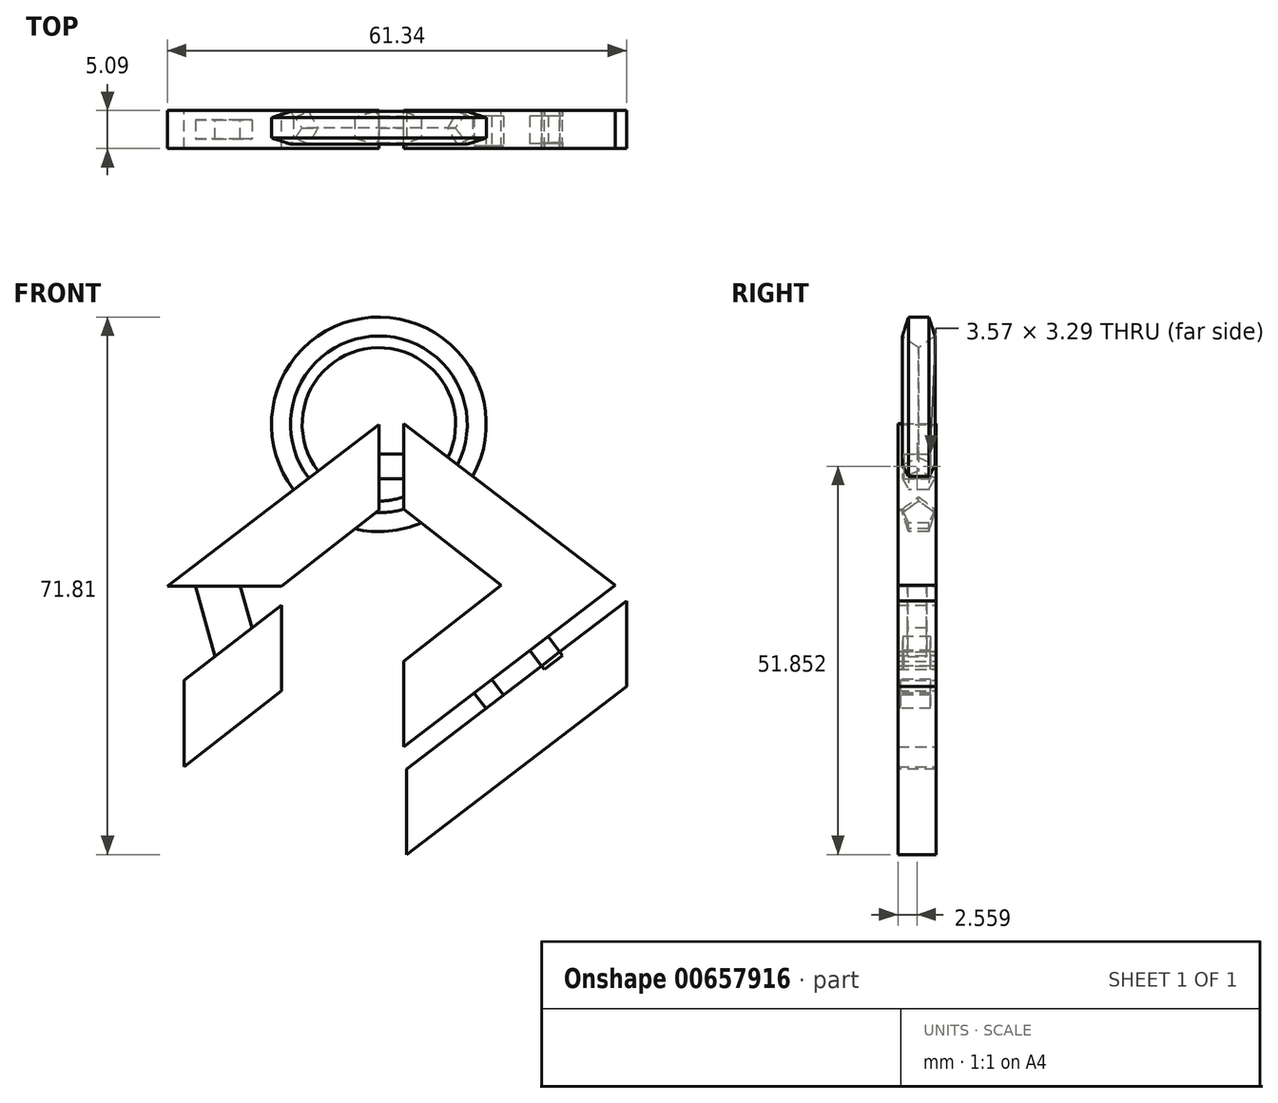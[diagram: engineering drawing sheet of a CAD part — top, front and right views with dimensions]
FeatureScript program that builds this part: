
annotation { "Feature Type Name" : "Feature", "Feature Type Description" : "" }
export const myFeature = defineFeature(function(context is Context, id is Id, definition is map)
    precondition{}
    {
        {
            var Q0;
            Q0=qCreatedBy(makeId("Front.planeOp"),FACE);
            var sketch = newSketch(context, id + "F0", { "sketchPlane" : qUnion([Q0])});
            skLineSegment(sketch, "E0", {"start": v(1.57, 49.1) * mm, "end": v(1.57, 37.68) * mm});
            skLineSegment(sketch, "E1", {"start": v(1.57, 37.68) * mm, "end": v(14.59, 27.51) * mm});
            skLineSegment(sketch, "E2", {"start": v(14.59, 27.51) * mm, "end": v(29.83, 27.51) * mm});
            skLineSegment(sketch, "E3", {"start": v(1.57, 49.1) * mm, "end": v(29.83, 27.51) * mm});
            skSolve(sketch);
        }
        {
            var Q0;
            Q0=makeQuery(id+"F0.imprint","IMPRINT",FACE,{"disambiguationData":[TD([[makeQuery(id+"F0.imprint","IMPRINT",EDGE,{"derivedFrom":sQuery(id+"F0.wireOp",EDGE,"E0")}),1.0]])]});
            extrude(context, id + "F1", {"entities" : qUnion([Q0]), "depth" : 5.08 * mm, "offsetDistance" : 25.4 * mm});
        }
        {
            var Q0;
            Q0=makeQuery(id+"F1.opExtrude","SWEPT_BODY",BODY,{"disambiguationData":[OSD([sQuery(id+"F0.wireOp",EDGE,"E0"),sQuery(id+"F0.wireOp",EDGE,"E1"),sQuery(id+"F0.wireOp",EDGE,"E2"),sQuery(id+"F0.wireOp",EDGE,"E3")])]});
            var Q1;
            Q1=makeQuery(id+"F1.opExtrude","SWEPT_FACE",FACE,{"disambiguationData":[OSD([sQuery(id+"F0.wireOp",EDGE,"E2")])]});
            mirror(context, id + "F2", {"operationType" : NewBodyOperationType.ADD, "entities" : qUnion([Q0]), "mirrorPlane" : qUnion([Q1])});
        }
        {
            var Q0;
            Q0=makeQuery(id+"F1.opExtrude","SWEPT_FACE",FACE,{"disambiguationData":[OSD([sQuery(id+"F0.wireOp",EDGE,"E0")])]});
            var sketch = newSketch(context, id + "F3", { "sketchPlane" : qUnion([Q0])});
            skLineSegment(sketch, "E4.bottom", {"start": v(4.3, 45.04) * mm, "end": v(0.74, 45.04) * mm});
            skLineSegment(sketch, "E4.top", {"start": v(4.3, 41.75) * mm, "end": v(0.74, 41.75) * mm});
            skLineSegment(sketch, "E4.left", {"start": v(4.3, 45.04) * mm, "end": v(4.3, 41.75) * mm});
            skLineSegment(sketch, "E4.right", {"start": v(0.74, 45.04) * mm, "end": v(0.74, 41.75) * mm});
            skPoint(sketch, "E4.middle", {"position": v(2.52, 43.4) * mm});
            skPoint(sketch, "E4.middle.positionSnap0", {"position": v(5.08, 43.4) * mm});
            skPoint(sketch, "E4.centerSnap0", {"position": v(5.08, 43.4) * mm});
            skSolve(sketch);
        }
        {
            var Q0;
            Q0=makeQuery(id+"F3.imprint","IMPRINT",FACE,{"disambiguationData":[TD([[makeQuery(id+"F3.imprint","IMPRINT",EDGE,{"derivedFrom":sQuery(id+"F3.wireOp",EDGE,"E4.bottom")}),1.0]])]});
            extrude(context, id + "F4", {"entities" : qUnion([Q0]), "operationType" : NewBodyOperationType.ADD, "depth" : 3.45 * mm, "offsetDistance" : 25.4 * mm});
        }
        {
            var Q0;
            Q0=qCreatedBy(makeId("Front.planeOp"),FACE);
            var sketch = newSketch(context, id + "F5", { "sketchPlane" : qUnion([Q0])});
            skLineSegment(sketch, "E5", {"start": v(0, 0) * mm, "end": v(-1.52, 0) * mm});
            skLineSegment(sketch, "E6", {"start": v(-1.74, 37.58) * mm, "end": v(-1.74, 49) * mm});
            skLineSegment(sketch, "E7", {"start": v(-1.74, 37.58) * mm, "end": v(-14.75, 27.42) * mm});
            skLineSegment(sketch, "E8", {"start": v(-14.75, 27.42) * mm, "end": v(-29.99, 27.42) * mm});
            skLineSegment(sketch, "E9", {"start": v(-29.99, 27.42) * mm, "end": v(-1.74, 49) * mm});
            skLineSegment(sketch, "E10", {"start": v(-14.75, 24.88) * mm, "end": v(-14.75, 13.45) * mm});
            skLineSegment(sketch, "E11", {"start": v(-14.75, 13.45) * mm, "end": v(-27.76, 3.28) * mm});
            skLineSegment(sketch, "E12", {"start": v(-27.76, 3.28) * mm, "end": v(-27.76, 14.82) * mm});
            skLineSegment(sketch, "E13", {"start": v(-27.76, 14.82) * mm, "end": v(-14.75, 24.88) * mm});
            skSolve(sketch);
        }
        {
            var Q0;
            Q0=makeQuery(id+"F5.imprint","IMPRINT",FACE,{"disambiguationData":[TD([[makeQuery(id+"F5.imprint","IMPRINT",EDGE,{"derivedFrom":sQuery(id+"F5.wireOp",EDGE,"E6")}),1.0]])]});
            var Q1;
            Q1=makeQuery(id+"F5.imprint","IMPRINT",FACE,{"disambiguationData":[TD([[makeQuery(id+"F5.imprint","IMPRINT",EDGE,{"derivedFrom":sQuery(id+"F5.wireOp",EDGE,"YTqawJW2-ZtEl-2KsG-vROz-UY6oSMgULrsX")}),-1.0]])]});
            extrude(context, id + "F6", {"entities" : qUnion([Q0, Q1]), "operationType" : NewBodyOperationType.ADD, "depth" : 5.08 * mm, "offsetDistance" : 25.4 * mm});
        }
        {
            var Q0;
            Q0=makeQuery(id+"F2.opPattern","COPY",FACE,{"derivedFrom":makeQuery(id+"F1.opExtrude","SWEPT_FACE",FACE,{"disambiguationData":[OSD([sQuery(id+"F0.wireOp",EDGE,"E3")])]}),"instanceName":"1"});
            var sketch = newSketch(context, id + "F7", { "sketchPlane" : qUnion([Q0])});
            skLineSegment(sketch, "E14.bottom", {"start": v(29.1, 0.71) * mm, "end": v(26.06, 0.71) * mm});
            skLineSegment(sketch, "E14.top", {"start": v(29.1, 4.41) * mm, "end": v(26.06, 4.41) * mm});
            skLineSegment(sketch, "E14.left", {"start": v(29.1, 0.71) * mm, "end": v(29.1, 4.41) * mm});
            skLineSegment(sketch, "E14.right", {"start": v(26.06, 0.71) * mm, "end": v(26.06, 4.41) * mm});
            skPoint(sketch, "E14.middle", {"position": v(27.58, 2.56) * mm});
            skLineSegment(sketch, "E15.bottom", {"start": v(19.67, 0.71) * mm, "end": v(16.7, 0.71) * mm});
            skLineSegment(sketch, "E15.top", {"start": v(19.67, 4.72) * mm, "end": v(16.7, 4.72) * mm});
            skLineSegment(sketch, "E15.left", {"start": v(19.67, 0.71) * mm, "end": v(19.67, 4.72) * mm});
            skLineSegment(sketch, "E15.right", {"start": v(16.7, 0.71) * mm, "end": v(16.7, 4.72) * mm});
            skPoint(sketch, "E15.middle", {"position": v(18.18, 2.72) * mm});
            skSolve(sketch);
        }
        {
            var Q0;
            Q0=makeQuery(id+"F7.imprint","IMPRINT",FACE,{"disambiguationData":[TD([[makeQuery(id+"F7.imprint","IMPRINT",EDGE,{"derivedFrom":sQuery(id+"F7.wireOp",EDGE,"E14.bottom")}),-1.0]])]});
            var Q1;
            Q1=makeQuery(id+"F7.imprint","IMPRINT",FACE,{"disambiguationData":[TD([[makeQuery(id+"F7.imprint","IMPRINT",EDGE,{"derivedFrom":sQuery(id+"F7.wireOp",EDGE,"E15.bottom")}),-1.0]])]});
            extrude(context, id + "F8", {"entities" : qUnion([Q0, Q1]), "operationType" : NewBodyOperationType.ADD, "depth" : 3.17 * mm, "offsetDistance" : 25.4 * mm});
        }
        {
            var Q0;
            Q0=makeQuery(id+"F8.opExtrude","SWEPT_FACE",FACE,{"disambiguationData":[OSD([sQuery(id+"F7.wireOp",EDGE,"E14.top")])]});
            var sketch = newSketch(context, id + "F9", { "sketchPlane" : qUnion([Q0])});
            skPoint(sketch, "E16", {"position": v(31.35, 25.43) * mm});
            skPoint(sketch, "E17", {"position": v(1.96, 2.97) * mm});
            skLineSegment(sketch, "E18", {"start": v(1.96, 2.97) * mm, "end": v(31.35, 25.43) * mm});
            skLineSegment(sketch, "E19", {"start": v(31.35, 25.43) * mm, "end": v(31.35, 14) * mm});
            skLineSegment(sketch, "E20", {"start": v(1.96, 2.97) * mm, "end": v(1.96, -8.46) * mm});
            skLineSegment(sketch, "E21", {"start": v(1.96, -8.46) * mm, "end": v(31.35, 14) * mm});
            skSolve(sketch);
        }
        {
            var Q0;
            Q0=makeQuery(id+"F9.imprint","IMPRINT",FACE,{"disambiguationData":[TD([[makeQuery(id+"F9.imprint","IMPRINT",EDGE,{"derivedFrom":sQuery(id+"F9.wireOp",EDGE,"E18")}),-1.0]])]});
            extrude(context, id + "F10", {"entities" : qUnion([Q0]), "oppositeDirection" : true, "depth" : 4.42 * mm, "offsetDistance" : 25.4 * mm});
        }
        {
            var Q0;
            Q0=makeQuery(id+"F10.opExtrude","CAP_FACE",FACE,{"disambiguationData":[OSD([sQuery(id+"F9.wireOp",EDGE,"E18"),sQuery(id+"F9.wireOp",EDGE,"E19"),sQuery(id+"F9.wireOp",EDGE,"E20"),sQuery(id+"F9.wireOp",EDGE,"E21")])],"isStart":true});
            extrude(context, id + "F11", {"entities" : qUnion([Q0]), "operationType" : NewBodyOperationType.ADD, "depth" : 0.66 * mm, "offsetDistance" : 25.4 * mm});
        }
        {
            var Q0;
            Q0=makeQuery(id+"F11.opExtrude","CAP_FACE",FACE,{"disambiguationData":[OSD([sQuery(id+"F7.wireOp",EDGE,"E14.top"),sQuery(id+"F7.wireOp",EDGE,"E14.left"),sQuery(id+"F7.wireOp",EDGE,"E14.right"),sQuery(id+"F9.wireOp",EDGE,"E18"),sQuery(id+"F9.wireOp",EDGE,"E19"),sQuery(id+"F9.wireOp",EDGE,"E20"),sQuery(id+"F9.wireOp",EDGE,"E21")])],"isStart":false});
            var sketch = newSketch(context, id + "F12", { "sketchPlane" : qUnion([Q0])});
            skLineSegment(sketch, "E22", {"start": v(20, 16.75) * mm, "end": v(22.42, 18.6) * mm});
            skLineSegment(sketch, "E23", {"start": v(22.42, 18.6) * mm, "end": v(22.78, 18.13) * mm});
            skLineSegment(sketch, "E24", {"start": v(22.78, 18.13) * mm, "end": v(20.35, 16.28) * mm});
            skLineSegment(sketch, "E25", {"start": v(20.35, 16.28) * mm, "end": v(20, 16.75) * mm});
            skSolve(sketch);
        }
        {
            var Q0;
            Q0=makeQuery(id+"F12.imprint","IMPRINT",FACE,{"disambiguationData":[TD([[makeQuery(id+"F12.imprint","IMPRINT",EDGE,{"derivedFrom":sQuery(id+"F12.wireOp",EDGE,"E22")}),-1.0]])]});
            extrude(context, id + "F13", {"entities" : qUnion([Q0]), "oppositeDirection" : true, "depth" : 0.76 * mm, "offsetDistance" : 25.4 * mm});
        }
        {
            var Q0;
            Q0=makeQuery(id+"F10.opExtrude","CAP_FACE",FACE,{"disambiguationData":[OSD([sQuery(id+"F7.wireOp",EDGE,"E14.top"),sQuery(id+"F7.wireOp",EDGE,"E14.left"),sQuery(id+"F7.wireOp",EDGE,"E14.right"),sQuery(id+"F9.wireOp",EDGE,"E18"),sQuery(id+"F9.wireOp",EDGE,"E19"),sQuery(id+"F9.wireOp",EDGE,"E20"),sQuery(id+"F9.wireOp",EDGE,"E21")])],"isStart":false});
            var sketch = newSketch(context, id + "F14", { "sketchPlane" : qUnion([Q0])});
            skLineSegment(sketch, "E26", {"start": v(-22.42, 18.6) * mm, "end": v(-20, 16.75) * mm});
            skLineSegment(sketch, "E27", {"start": v(-20, 16.75) * mm, "end": v(-20.35, 16.28) * mm});
            skLineSegment(sketch, "E28", {"start": v(-20.35, 16.28) * mm, "end": v(-22.78, 18.13) * mm});
            skLineSegment(sketch, "E29", {"start": v(-22.78, 18.13) * mm, "end": v(-22.42, 18.6) * mm});
            skSolve(sketch);
        }
        {
            var Q0;
            Q0=makeQuery(id+"F14.imprint","IMPRINT",FACE,{"disambiguationData":[TD([[makeQuery(id+"F14.imprint","IMPRINT",EDGE,{"derivedFrom":sQuery(id+"F14.wireOp",EDGE,"E26")}),-1.0]])]});
            extrude(context, id + "F15", {"entities" : qUnion([Q0]), "oppositeDirection" : true, "depth" : 5.08 * mm, "offsetDistance" : 25.4 * mm});
        }
        {
            var Q0;
            Q0=makeQuery(id+"F1.opExtrude","SWEPT_FACE",FACE,{"disambiguationData":[OSD([sQuery(id+"F0.wireOp",EDGE,"E3")])]});
            var sketch = newSketch(context, id + "F16", { "sketchPlane" : qUnion([Q0])});
            skCircle(sketch, "E30.cCircle", {"center": v(-18.82, -2.3) * mm, "radius": 1.86 * mm, "construction": true});
            skLineSegment(sketch, "E30.0", {"start": v(-16.96, -0.95) * mm, "end": v(-16.96, -3.65) * mm});
            skLineSegment(sketch, "E30.1", {"start": v(-16.96, -3.65) * mm, "end": v(-19.53, -4.48) * mm});
            skLineSegment(sketch, "E30.2", {"start": v(-19.53, -4.48) * mm, "end": v(-21.12, -2.3) * mm});
            skLineSegment(sketch, "E30.3", {"start": v(-21.12, -2.3) * mm, "end": v(-19.53, -0.12) * mm});
            skLineSegment(sketch, "E30.4", {"start": v(-19.53, -0.12) * mm, "end": v(-16.96, -0.95) * mm});
            skPoint(sketch, "E30.0.midPoint", {"position": v(-16.96, -2.3) * mm});
            skSolve(sketch);
        }
        {
            var Q0;
            Q0=makeQuery(id+"F16.imprint","IMPRINT",FACE,{"disambiguationData":[TD([[makeQuery(id+"F16.imprint","IMPRINT",EDGE,{"derivedFrom":sQuery(id+"F16.wireOp",EDGE,"E30.0")}),-1.0]])]});
            var Q1;
            Q1=makeQuery(id+"F6.opExtrude","SWEPT_EDGE",EDGE,{"disambiguationData":[OSD([sQuery(id+"F5.wireOp",EDGE,"E6"),sQuery(id+"F5.wireOp",EDGE,"E9")])]});
            revolve(context, id + "F17", {"operationType" : NewBodyOperationType.ADD, "entities" : qUnion([Q0]), "axis" : qUnion([Q1]), "revolveType" : RevolveType.FULL});
        }
        {
            var Q0;
            Q0=makeQuery(id+"F6.opExtrude","CAP_FACE",FACE,{"disambiguationData":[OSD([sQuery(id+"F5.wireOp",EDGE,"E6"),sQuery(id+"F5.wireOp",EDGE,"E7"),sQuery(id+"F5.wireOp",EDGE,"E8"),sQuery(id+"F5.wireOp",EDGE,"E9")])],"isStart":false});
            cPlane(context, id + "F18", {"entities" : qUnion([Q0]), "cplaneType" : CPlaneType.OFFSET, "offset" : 2.54 * mm, "oppositeDirection" : true, "width" : 152.4 * mm, "height" : 152.4 * mm});
        }
        {
            var Q0;
            Q0=makeQuery(id+"F5.imprint","IMPRINT",FACE,{"disambiguationData":[TD([[makeQuery(id+"F5.imprint","IMPRINT",EDGE,{"derivedFrom":sQuery(id+"F5.wireOp",EDGE,"E10")}),-1.0]])]});
            extrude(context, id + "F19", {"entities" : qUnion([Q0]), "depth" : 5.08 * mm, "offsetDistance" : 25.4 * mm});
        }
        {
            var Q0;
            Q0=qCreatedBy(id+"F18.planeOp",FACE);
            var sketch = newSketch(context, id + "F20", { "sketchPlane" : qUnion([Q0])});
            skLineSegment(sketch, "E31", {"start": v(-26.34, 27.7) * mm, "end": v(-23.46, 17.42) * mm});
            skLineSegment(sketch, "E32", {"start": v(-23.46, 17.42) * mm, "end": v(-18.62, 21.58) * mm});
            skLineSegment(sketch, "E33", {"start": v(-18.62, 21.58) * mm, "end": v(-20.3, 27.54) * mm});
            skLineSegment(sketch, "E34", {"start": v(-20.3, 27.54) * mm, "end": v(-26.34, 27.7) * mm});
            skSolve(sketch);
        }
        {
            var Q0;
            Q0=makeQuery(id+"F20.imprint","IMPRINT",FACE,{"disambiguationData":[TD([[makeQuery(id+"F20.imprint","IMPRINT",EDGE,{"derivedFrom":sQuery(id+"F20.wireOp",EDGE,"E31")}),1.0]])]});
            extrude(context, id + "F21", {"entities" : qUnion([Q0]), "operationType" : NewBodyOperationType.ADD, "depth" : 1.27 * mm, "offsetDistance" : 25.4 * mm});
        }
        {
            var Q0;
            Q0=makeQuery(id+"F21.opExtrude","CAP_FACE",FACE,{"disambiguationData":[OSD([sQuery(id+"F20.wireOp",EDGE,"E31"),sQuery(id+"F20.wireOp",EDGE,"E32"),sQuery(id+"F20.wireOp",EDGE,"E33"),sQuery(id+"F20.wireOp",EDGE,"E34")])],"isStart":true});
            extrude(context, id + "F22", {"entities" : qUnion([Q0]), "operationType" : NewBodyOperationType.ADD, "depth" : 1.27 * mm, "offsetDistance" : 25.4 * mm});
        }
        {
            var Q0;
            Q0=makeQuery(id+"F5.imprint","IMPRINT",FACE,{"disambiguationData":[TD([[makeQuery(id+"F5.imprint","IMPRINT",EDGE,{"derivedFrom":sQuery(id+"F5.wireOp",EDGE,"E10")}),-1.0]])]});
            extrude(context, id + "F23", {"entities" : qUnion([Q0]), "operationType" : NewBodyOperationType.ADD, "depth" : 5.08 * mm, "offsetDistance" : 25.4 * mm});
        }
    });
